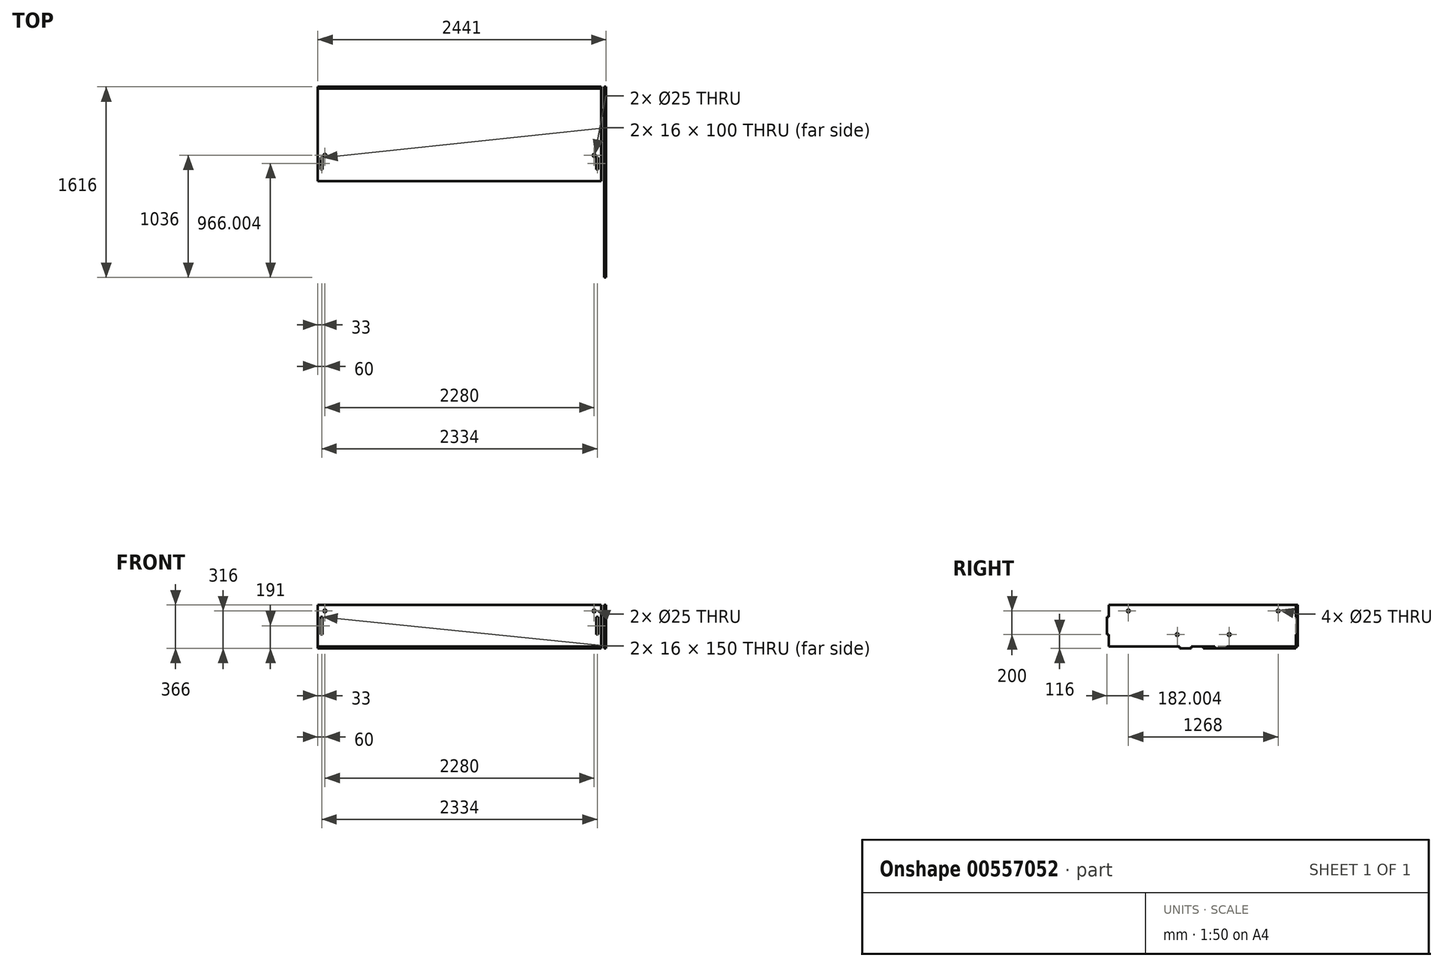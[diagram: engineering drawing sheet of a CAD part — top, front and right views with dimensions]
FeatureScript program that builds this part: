
annotation { "Feature Type Name" : "Feature", "Feature Type Description" : "" }
export const myFeature = defineFeature(function(context is Context, id is Id, definition is map)
    precondition{}
    {
        {
            var Q0;
            Q0=qCreatedBy(makeId("Top.planeOp"),FACE);
            var sketch = newSketch(context, id + "F0", { "sketchPlane" : qUnion([Q0])});
            skLineSegment(sketch, "E0.bottom", {"start": v(-878.64, 91.32) * mm, "end": v(1521.36, 91.32) * mm});
            skLineSegment(sketch, "E0.top", {"start": v(-878.64, 875.32) * mm, "end": v(1521.36, 875.32) * mm});
            skLineSegment(sketch, "E0.left", {"start": v(-878.64, 91.32) * mm, "end": v(-878.64, 875.32) * mm});
            skLineSegment(sketch, "E0.right", {"start": v(1521.36, 91.32) * mm, "end": v(1521.36, 875.32) * mm});
            skLineSegment(sketch, "E1", {"start": v(-853.64, 875.32) * mm, "end": v(-853.64, 91.32) * mm, "construction": true});
            skLineSegment(sketch, "E2", {"start": v(-837.64, 875.32) * mm, "end": v(-837.64, 91.32) * mm, "construction": true});
            skLineSegment(sketch, "E3", {"start": v(1480.36, 875.32) * mm, "end": v(1480.36, 91.32) * mm, "construction": true});
            skLineSegment(sketch, "E4", {"start": v(1496.36, 875.32) * mm, "end": v(1496.36, 91.32) * mm, "construction": true});
            skLineSegment(sketch, "E5", {"start": v(1480.36, 191.32) * mm, "end": v(1496.36, 191.32) * mm});
            skLineSegment(sketch, "E6", {"start": v(1496.36, 291.32) * mm, "end": v(1480.36, 291.32) * mm});
            skLineSegment(sketch, "E7", {"start": v(-853.64, 191.32) * mm, "end": v(-837.64, 191.32) * mm});
            skLineSegment(sketch, "E8", {"start": v(-853.64, 291.32) * mm, "end": v(-837.64, 291.32) * mm});
            skLineSegment(sketch, "E9", {"start": v(1480.36, 291.32) * mm, "end": v(1480.36, 191.32) * mm});
            skLineSegment(sketch, "E10", {"start": v(1496.36, 191.32) * mm, "end": v(1496.36, 291.32) * mm});
            skLineSegment(sketch, "E11", {"start": v(-853.64, 291.32) * mm, "end": v(-853.64, 191.32) * mm});
            skLineSegment(sketch, "E12", {"start": v(-837.64, 191.32) * mm, "end": v(-837.64, 291.32) * mm});
            skPoint(sketch, "E13", {"position": v(-818.64, 311.32) * mm});
            skCircle(sketch, "E14", {"center": v(-818.64, 311.32) * mm, "radius": 12.5 * mm});
            skPoint(sketch, "E15", {"position": v(1461.36, 311.32) * mm});
            skCircle(sketch, "E16", {"center": v(1461.36, 311.32) * mm, "radius": 12.5 * mm});
            skSolve(sketch);
        }
        {
            var Q0;
            Q0=makeQuery(id+"F0.imprint","IMPRINT",FACE,{"disambiguationData":[TD([[makeQuery(id+"F0.imprint","IMPRINT",EDGE,{"derivedFrom":sQuery(id+"F0.wireOp",EDGE,"E0.top")}),-1.0]])]});
            extrude(context, id + "F1", {"entities" : qUnion([Q0]), "depth" : 16 * mm, "offsetDistance" : 25 * mm});
        }
        {
            var Q0;
            Q0=makeQuery(id+"F1.opExtrude","SWEPT_FACE",FACE,{"disambiguationData":[OSD([sQuery(id+"F0.wireOp",EDGE,"E0.top")])]});
            var sketch = newSketch(context, id + "F2", { "sketchPlane" : qUnion([Q0])});
            skLineSegment(sketch, "E17.bottom", {"start": v(878.64, 16) * mm, "end": v(-1521.36, 16) * mm});
            skLineSegment(sketch, "E17.top", {"start": v(878.64, 366) * mm, "end": v(-1521.36, 366) * mm});
            skLineSegment(sketch, "E17.left", {"start": v(878.64, 16) * mm, "end": v(878.64, 366) * mm});
            skLineSegment(sketch, "E17.right", {"start": v(-1521.36, 16) * mm, "end": v(-1521.36, 366) * mm});
            skPoint(sketch, "E18", {"position": v(-1496.36, 16) * mm});
            skPoint(sketch, "E19", {"position": v(-1480.36, 16) * mm});
            skLineSegment(sketch, "E20", {"start": v(-1496.36, 16) * mm, "end": v(-1496.36, 366) * mm, "construction": true});
            skLineSegment(sketch, "E21", {"start": v(-1480.36, 16) * mm, "end": v(-1480.36, 366) * mm, "construction": true});
            skPoint(sketch, "E22", {"position": v(-1480.36, 266) * mm});
            skPoint(sketch, "E23", {"position": v(-1480.36, 116) * mm});
            skLineSegment(sketch, "E24", {"start": v(-1480.36, 116) * mm, "end": v(-1480.36, 266) * mm});
            skLineSegment(sketch, "E25", {"start": v(-1496.28, 266) * mm, "end": v(-1496.36, 116) * mm});
            skLineSegment(sketch, "E26", {"start": v(-1496.36, 116) * mm, "end": v(-1480.36, 116) * mm});
            skLineSegment(sketch, "E27", {"start": v(-1480.36, 266) * mm, "end": v(-1496.28, 266) * mm});
            skPoint(sketch, "E28", {"position": v(853.64, 16) * mm});
            skPoint(sketch, "E29", {"position": v(837.64, 16) * mm});
            skLineSegment(sketch, "E30", {"start": v(853.64, 16) * mm, "end": v(853.64, 366) * mm, "construction": true});
            skLineSegment(sketch, "E31", {"start": v(837.64, 16) * mm, "end": v(837.64, 366) * mm, "construction": true});
            skPoint(sketch, "E32", {"position": v(853.64, 116) * mm});
            skPoint(sketch, "E33", {"position": v(853.64, 266) * mm});
            skLineSegment(sketch, "E34", {"start": v(853.64, 116) * mm, "end": v(837.64, 116) * mm});
            skLineSegment(sketch, "E35", {"start": v(853.64, 266) * mm, "end": v(837.64, 266) * mm});
            skLineSegment(sketch, "E36", {"start": v(837.64, 266) * mm, "end": v(837.64, 116) * mm});
            skPoint(sketch, "E37", {"position": v(818.64, 316) * mm});
            skCircle(sketch, "E38", {"center": v(818.64, 316) * mm, "radius": 12.5 * mm});
            skLineSegment(sketch, "E39", {"start": v(853.64, 116) * mm, "end": v(853.64, 266) * mm});
            skPoint(sketch, "E40", {"position": v(-1461.36, 316) * mm});
            skCircle(sketch, "E41", {"center": v(-1461.36, 316) * mm, "radius": 12.5 * mm});
            skSolve(sketch);
        }
        {
            var Q0;
            Q0=makeQuery(id+"F2.imprint","IMPRINT",FACE,{"disambiguationData":[TD([[makeQuery(id+"F2.imprint","IMPRINT",EDGE,{"derivedFrom":sQuery(id+"F2.wireOp",EDGE,"E17.bottom")}),-1.0]])]});
            extrude(context, id + "F3", {"entities" : qUnion([Q0]), "depth" : 16 * mm, "offsetDistance" : 25 * mm});
        }
        {
            var Q0;
            Q0=makeQuery(id+"F1.opExtrude","SWEPT_FACE",FACE,{"disambiguationData":[OSD([sQuery(id+"F0.wireOp",EDGE,"E0.right")])]});
            cPlane(context, id + "F4", {"entities" : qUnion([Q0]), "cplaneType" : CPlaneType.OFFSET, "offset" : 25 * mm, "width" : 150 * mm, "height" : 150 * mm});
        }
        {
            var Q0;
            Q0=qCreatedBy(id+"F4.planeOp",FACE);
            var sketch = newSketch(context, id + "F5", { "sketchPlane" : qUnion([Q0])});
            skLineSegment(sketch, "E42.bottom", {"start": v(91.32, 16) * mm, "end": v(875.32, 16) * mm, "construction": true});
            skLineSegment(sketch, "E42.top", {"start": v(91.32, 366) * mm, "end": v(875.32, 366) * mm, "construction": true});
            skLineSegment(sketch, "E42.left", {"start": v(91.32, 16) * mm, "end": v(91.32, 366) * mm, "construction": true});
            skLineSegment(sketch, "E42.right", {"start": v(875.32, 16) * mm, "end": v(875.32, 366) * mm, "construction": true});
            skLineSegment(sketch, "E43", {"start": v(191.32, 16) * mm, "end": v(191.32, 0) * mm});
            skLineSegment(sketch, "E44", {"start": v(191.32, 0) * mm, "end": v(291.32, 0) * mm});
            skLineSegment(sketch, "E45", {"start": v(291.32, 0) * mm, "end": v(291.32, 16) * mm});
            skLineSegment(sketch, "E46", {"start": v(311.32, 16) * mm, "end": v(311.32, 116) * mm, "construction": true});
            skLineSegment(sketch, "E47", {"start": v(311.32, 16) * mm, "end": v(311.32, 0) * mm, "construction": true});
            skCircle(sketch, "E48", {"center": v(311.32, 116) * mm, "radius": 12.5 * mm});
            skLineSegment(sketch, "E49", {"start": v(875.32, 116) * mm, "end": v(891.32, 116) * mm});
            skLineSegment(sketch, "E50", {"start": v(891.32, 116) * mm, "end": v(891.32, 266) * mm});
            skLineSegment(sketch, "E51", {"start": v(891.32, 266) * mm, "end": v(875.32, 266) * mm});
            skLineSegment(sketch, "E52", {"start": v(725.32, 316) * mm, "end": v(875.32, 316) * mm, "construction": true});
            skCircle(sketch, "E53", {"center": v(725.32, 316) * mm, "radius": 12.5 * mm});
            skLineSegment(sketch, "E54", {"start": v(191.32, 16) * mm, "end": v(91.32, 16) * mm});
            skLineSegment(sketch, "E55", {"start": v(91.32, 366) * mm, "end": v(875.32, 366) * mm});
            skLineSegment(sketch, "E56", {"start": v(875.32, 366) * mm, "end": v(875.32, 266) * mm});
            skLineSegment(sketch, "E57", {"start": v(875.32, 116) * mm, "end": v(875.32, 16) * mm});
            skLineSegment(sketch, "E58", {"start": v(875.32, 16) * mm, "end": v(291.32, 16) * mm});
            skLineSegment(sketch, "E59.MirrorCS", {"start": v(91.32, 366) * mm, "end": v(-708.68, 366) * mm});
            skLineSegment(sketch, "E60.MirrorCS", {"start": v(91.32, 16) * mm, "end": v(-708.68, 16) * mm, "construction": true});
            skLineSegment(sketch, "E61.MirrorCS", {"start": v(-8.68, 0) * mm, "end": v(-108.68, 0) * mm});
            skLineSegment(sketch, "E62.MirrorCS", {"start": v(-8.68, 16) * mm, "end": v(91.32, 16) * mm});
            skLineSegment(sketch, "E63.MirrorCS", {"start": v(-108.68, 0) * mm, "end": v(-108.68, 16) * mm});
            skLineSegment(sketch, "E64.MirrorCS", {"start": v(-8.68, 16) * mm, "end": v(-8.68, 0) * mm});
            skLineSegment(sketch, "E65.MirrorCS", {"start": v(-708.68, 16) * mm, "end": v(-108.68, 16) * mm});
            skLineSegment(sketch, "E66.MirrorCS", {"start": v(-708.68, 116) * mm, "end": v(-708.68, 16) * mm});
            skLineSegment(sketch, "E67.MirrorCS", {"start": v(-708.68, 116) * mm, "end": v(-724.68, 116) * mm});
            skLineSegment(sketch, "E68.MirrorCS", {"start": v(-724.68, 116) * mm, "end": v(-724.68, 266) * mm});
            skLineSegment(sketch, "E69.MirrorCS", {"start": v(-708.68, 366) * mm, "end": v(-708.68, 266) * mm});
            skCircle(sketch, "E70.MirrorC", {"center": v(-128.68, 116) * mm, "radius": 12.5 * mm});
            skCircle(sketch, "E71.MirrorC", {"center": v(-542.68, 316) * mm, "radius": 12.5 * mm});
            skLineSegment(sketch, "E72", {"start": v(-708.68, 266) * mm, "end": v(-724.68, 266) * mm});
            skSolve(sketch);
        }
        {
            var Q0;
            Q0=makeQuery(id+"F5.imprint","IMPRINT",FACE,{"disambiguationData":[TD([[makeQuery(id+"F5.imprint","IMPRINT",EDGE,{"derivedFrom":sQuery(id+"F5.wireOp",EDGE,"E43")}),1.0]])]});
            extrude(context, id + "F6", {"entities" : qUnion([Q0]), "depth" : 16 * mm, "offsetDistance" : 25 * mm});
        }
    });
